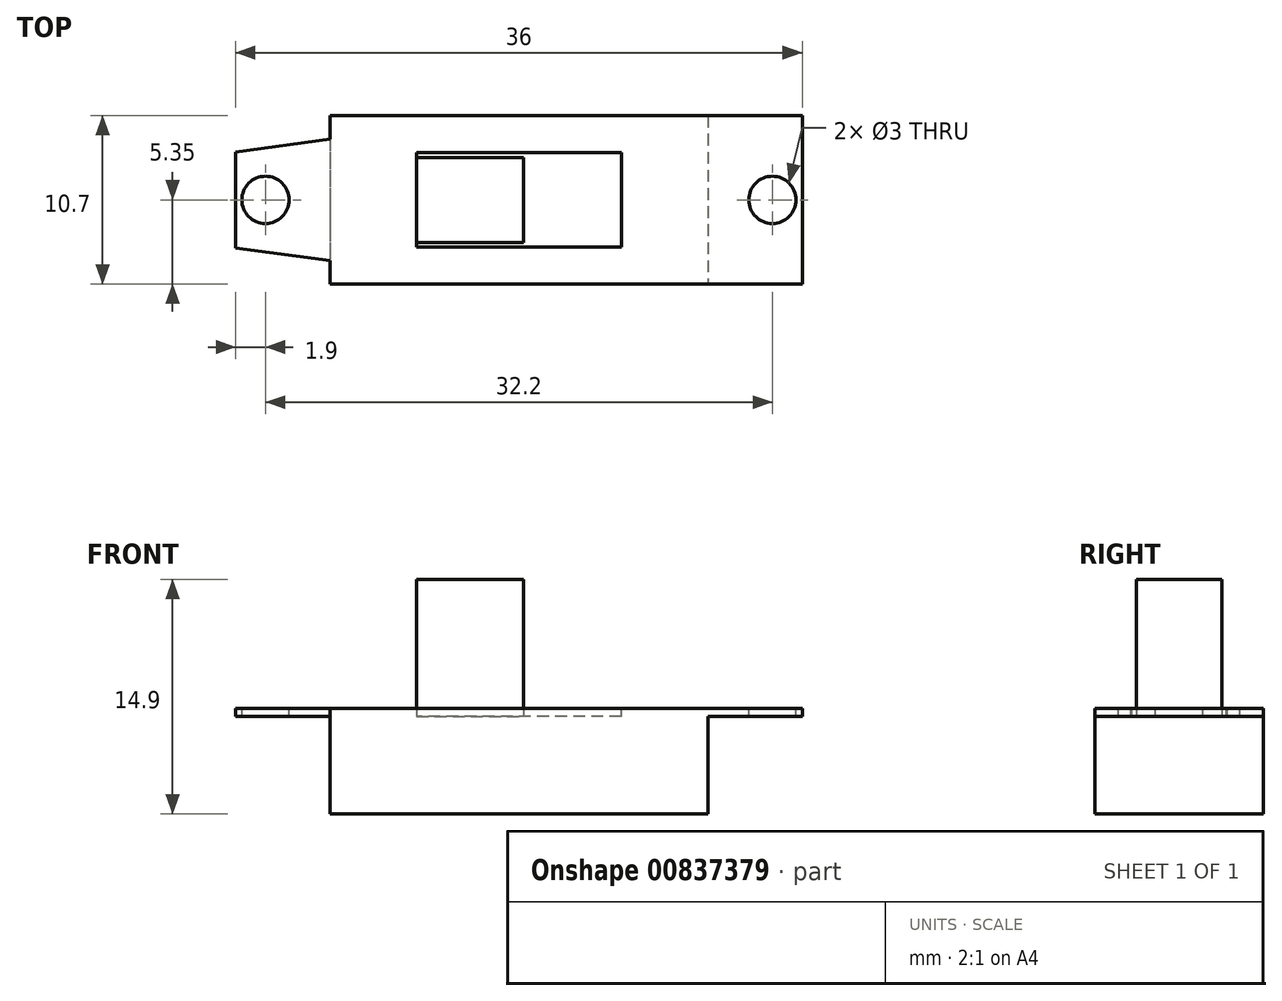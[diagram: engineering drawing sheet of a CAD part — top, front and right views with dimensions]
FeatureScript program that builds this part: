
annotation { "Feature Type Name" : "Feature", "Feature Type Description" : "" }
export const myFeature = defineFeature(function(context is Context, id is Id, definition is map)
    precondition{}
    {
        {
            var Q0;
            Q0=qCreatedBy(makeId("Top.planeOp"),FACE);
            var sketch = newSketch(context, id + "F0", { "sketchPlane" : qUnion([Q0])});
            skLineSegment(sketch, "E0.bottom", {"start": v(18, 5.35) * mm, "end": v(-18, 5.35) * mm});
            skLineSegment(sketch, "E0.top", {"start": v(18, -5.35) * mm, "end": v(-18, -5.35) * mm});
            skLineSegment(sketch, "E0.left", {"start": v(18, 5.35) * mm, "end": v(18, -5.35) * mm});
            skLineSegment(sketch, "E0.right", {"start": v(-18, 5.35) * mm, "end": v(-18, -5.35) * mm});
            skPoint(sketch, "E0.middle", {"position": v(0, 0) * mm});
            skSolve(sketch);
        }
        {
            var Q0;
            Q0=makeQuery(id+"F0.imprint","IMPRINT",FACE,{"disambiguationData":[TD([[makeQuery(id+"F0.imprint","IMPRINT",EDGE,{"derivedFrom":sQuery(id+"F0.wireOp",EDGE,"E0.bottom")}),1.0]])]});
            extrude(context, id + "F1", {"entities" : qUnion([Q0]), "depth" : 0.5 * mm, "offsetDistance" : 25 * mm});
        }
        {
            var Q0;
            Q0=makeQuery(id+"F1.opExtrude","CAP_FACE",FACE,{"disambiguationData":[OSD([sQuery(id+"F0.wireOp",EDGE,"E0.bottom"),sQuery(id+"F0.wireOp",EDGE,"E0.top"),sQuery(id+"F0.wireOp",EDGE,"E0.left"),sQuery(id+"F0.wireOp",EDGE,"E0.right")])],"isStart":true});
            var sketch = newSketch(context, id + "F2", { "sketchPlane" : qUnion([Q0])});
            skLineSegment(sketch, "E1.bottom", {"start": v(12, -5.35) * mm, "end": v(-12, -5.35) * mm});
            skLineSegment(sketch, "E1.top", {"start": v(12, 5.35) * mm, "end": v(-12, 5.35) * mm});
            skLineSegment(sketch, "E1.left", {"start": v(12, -5.35) * mm, "end": v(12, 5.35) * mm});
            skLineSegment(sketch, "E1.right", {"start": v(-12, -5.35) * mm, "end": v(-12, 5.35) * mm});
            skPoint(sketch, "E1.middle", {"position": v(0, 0) * mm});
            skSolve(sketch);
        }
        {
            var Q0;
            Q0=makeQuery(id+"F2.imprint","IMPRINT",FACE,{"disambiguationData":[TD([[makeQuery(id+"F2.imprint","IMPRINT",EDGE,{"derivedFrom":sQuery(id+"F2.wireOp",EDGE,"E1.bottom")}),-1.0]])]});
            extrude(context, id + "F3", {"entities" : qUnion([Q0]), "operationType" : NewBodyOperationType.ADD, "depth" : 6.2 * mm, "offsetDistance" : 25 * mm});
        }
        {
            var Q0;
            Q0=makeQuery(id+"F1.opExtrude","CAP_FACE",FACE,{"disambiguationData":[OSD([sQuery(id+"F0.wireOp",EDGE,"E0.bottom"),sQuery(id+"F0.wireOp",EDGE,"E0.top"),sQuery(id+"F0.wireOp",EDGE,"E0.left"),sQuery(id+"F0.wireOp",EDGE,"E0.right")])],"isStart":false});
            var sketch = newSketch(context, id + "F4", { "sketchPlane" : qUnion([Q0])});
            skLineSegment(sketch, "E2.bottom", {"start": v(6.5, 3) * mm, "end": v(-6.5, 3) * mm});
            skLineSegment(sketch, "E2.top", {"start": v(6.5, -3) * mm, "end": v(-6.5, -3) * mm});
            skLineSegment(sketch, "E2.left", {"start": v(6.5, 3) * mm, "end": v(6.5, -3) * mm});
            skLineSegment(sketch, "E2.right", {"start": v(-6.5, 3) * mm, "end": v(-6.5, -3) * mm});
            skPoint(sketch, "E2.middle", {"position": v(0, 0) * mm});
            skSolve(sketch);
        }
        {
            var Q0;
            Q0=makeQuery(id+"F4.imprint","IMPRINT",FACE,{"disambiguationData":[TD([[makeQuery(id+"F4.imprint","IMPRINT",EDGE,{"derivedFrom":sQuery(id+"F4.wireOp",EDGE,"E2.bottom")}),1.0]])]});
            extrude(context, id + "F5", {"entities" : qUnion([Q0]), "operationType" : NewBodyOperationType.REMOVE, "oppositeDirection" : true, "depth" : 0.5 * mm, "offsetDistance" : 25 * mm});
        }
        {
            var Q0;
            Q0=makeQuery(id+"F5.boolean.opBoolean","COPY",FACE,{"derivedFrom":makeQuery(id+"F5.opExtrude","CAP_FACE",FACE,{"disambiguationData":[OSD([sQuery(id+"F4.wireOp",EDGE,"E2.bottom"),sQuery(id+"F4.wireOp",EDGE,"E2.top"),sQuery(id+"F4.wireOp",EDGE,"E2.left"),sQuery(id+"F4.wireOp",EDGE,"E2.right")])],"isStart":false})});
            var sketch = newSketch(context, id + "F6", { "sketchPlane" : qUnion([Q0])});
            skLineSegment(sketch, "E3.bottom", {"start": v(-6.5, 2.7) * mm, "end": v(0.3, 2.7) * mm});
            skLineSegment(sketch, "E3.top", {"start": v(-6.5, -2.7) * mm, "end": v(0.3, -2.7) * mm});
            skLineSegment(sketch, "E3.left", {"start": v(-6.5, 2.7) * mm, "end": v(-6.5, -2.7) * mm});
            skLineSegment(sketch, "E3.right", {"start": v(0.3, 2.7) * mm, "end": v(0.3, -2.7) * mm});
            skLineSegment(sketch, "E4", {"start": v(0, 0) * mm, "end": v(-3.24, 0) * mm, "construction": true});
            skPoint(sketch, "E5", {"position": v(0.3, 0) * mm});
            skSolve(sketch);
        }
        {
            var Q0;
            Q0=makeQuery(id+"F6.imprint","IMPRINT",FACE,{"disambiguationData":[TD([[makeQuery(id+"F6.imprint","IMPRINT",EDGE,{"derivedFrom":sQuery(id+"F6.wireOp",EDGE,"E3.bottom")}),-1.0]])]});
            extrude(context, id + "F7", {"entities" : qUnion([Q0]), "operationType" : NewBodyOperationType.ADD, "depth" : 8.7 * mm, "offsetDistance" : 25 * mm});
        }
        {
            var Q0;
            Q0=makeQuery(id+"F1.opExtrude","CAP_FACE",FACE,{"disambiguationData":[OSD([sQuery(id+"F0.wireOp",EDGE,"E0.bottom"),sQuery(id+"F0.wireOp",EDGE,"E0.top"),sQuery(id+"F0.wireOp",EDGE,"E0.left"),sQuery(id+"F0.wireOp",EDGE,"E0.right")])],"isStart":false});
            var sketch = newSketch(context, id + "F8", { "sketchPlane" : qUnion([Q0])});
            skCircle(sketch, "E6", {"center": v(-16.1, 0) * mm, "radius": 1.5 * mm});
            skCircle(sketch, "E7", {"center": v(16.1, 0) * mm, "radius": 1.5 * mm});
            skSolve(sketch);
        }
        {
            var Q0;
            Q0=makeQuery(id+"F8.imprint","IMPRINT",FACE,{"disambiguationData":[TD([[makeQuery(id+"F8.imprint","IMPRINT",EDGE,{"derivedFrom":sQuery(id+"F8.wireOp",EDGE,"E6")}),1.0]])]});
            var Q1;
            Q1=makeQuery(id+"F8.imprint","IMPRINT",FACE,{"disambiguationData":[TD([[makeQuery(id+"F8.imprint","IMPRINT",EDGE,{"derivedFrom":sQuery(id+"F8.wireOp",EDGE,"E7")}),1.0]])]});
            extrude(context, id + "F9", {"entities" : qUnion([Q0, Q1]), "operationType" : NewBodyOperationType.REMOVE, "endBound" : BoundingType.UP_TO_NEXT, "oppositeDirection" : true, "depth" : 25 * mm, "offsetDistance" : 25 * mm});
        }
        {
            var Q0;
            Q0=makeQuery(id+"F1.opExtrude","CAP_FACE",FACE,{"disambiguationData":[OSD([sQuery(id+"F0.wireOp",EDGE,"E0.bottom"),sQuery(id+"F0.wireOp",EDGE,"E0.top"),sQuery(id+"F0.wireOp",EDGE,"E0.left"),sQuery(id+"F0.wireOp",EDGE,"E0.right")])],"isStart":false});
            var sketch = newSketch(context, id + "F10", { "sketchPlane" : qUnion([Q0])});
            skLineSegment(sketch, "E8", {"start": v(-12, 5.35) * mm, "end": v(-12, 3.85) * mm});
            skLineSegment(sketch, "E9", {"start": v(-12, 3.85) * mm, "end": v(-18, 3.05) * mm});
            skLineSegment(sketch, "E10", {"start": v(-18, 3.05) * mm, "end": v(-18, 5.35) * mm});
            skLineSegment(sketch, "E11", {"start": v(-18, 5.35) * mm, "end": v(-12, 5.35) * mm});
            skLineSegment(sketch, "E12", {"start": v(-18, -3.05) * mm, "end": v(-12, -3.85) * mm});
            skLineSegment(sketch, "E13", {"start": v(-12, -3.85) * mm, "end": v(-12, -5.35) * mm});
            skLineSegment(sketch, "E14", {"start": v(-12, -5.35) * mm, "end": v(-18, -5.35) * mm});
            skLineSegment(sketch, "E15", {"start": v(-18, -5.35) * mm, "end": v(-18, -3.05) * mm});
            skLineSegment(sketch, "E16", {"start": v(-18, 3.05) * mm, "end": v(-18, -3.05) * mm, "construction": true});
            skLineSegment(sketch, "E17", {"start": v(-16.1, 0) * mm, "end": v(-21.16, 0) * mm, "construction": true});
            skPoint(sketch, "E18", {"position": v(-18, 0) * mm});
            skSolve(sketch);
        }
        {
            var Q0;
            Q0=makeQuery(id+"F10.imprint","IMPRINT",FACE,{"disambiguationData":[TD([[makeQuery(id+"F10.imprint","IMPRINT",EDGE,{"derivedFrom":sQuery(id+"F10.wireOp",EDGE,"E8")}),-1.0]])]});
            var Q1;
            Q1=makeQuery(id+"F10.imprint","IMPRINT",FACE,{"disambiguationData":[TD([[makeQuery(id+"F10.imprint","IMPRINT",EDGE,{"derivedFrom":sQuery(id+"F10.wireOp",EDGE,"E12")}),-1.0]])]});
            extrude(context, id + "F11", {"entities" : qUnion([Q0, Q1]), "operationType" : NewBodyOperationType.REMOVE, "endBound" : BoundingType.UP_TO_NEXT, "oppositeDirection" : true, "depth" : 25 * mm, "offsetDistance" : 25 * mm});
        }
    });
